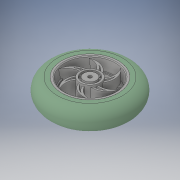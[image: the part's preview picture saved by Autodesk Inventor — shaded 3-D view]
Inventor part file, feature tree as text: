
AUTODESK INVENTOR PART (.ipt)
format: ipt  version: 2018 (Build 220112000, 112)  size: 624,640 bytes
history: native  units: in
note: dims shown in document units (in); Inventor stores cm internally (conversion verified against a paired STEP export)
features: sketch x11, extrude x9, plane x2, revolve x2, mirror x1, chamfer x1, projected_geometry x1
ambient origin geometry x8: Origin, YZ Plane, XZ Plane, XY Plane, X Axis, Y Axis, Z Axis, Center Point
bodies: Solid1 (feature_tree), Solid2 (feature_tree)
feature tree (27):
  extrude  "Extrusion1"  Depth=0.748in TaperAngle=0.0deg
  extrude  "Extrusion2"  Depth=0.748in TaperAngle=0.0deg
  extrude  "Extrusion3"  Depth=0.748in TaperAngle=0.0deg
  extrude  "Extrusion4"  Depth=0.748in TaperAngle=0.0deg
  plane  "Work Plane1"
  extrude  "Extrusion5"  Depth=0.6299in TaperAngle=0.0deg
  extrude  "Extrusion6"  Depth=0.2165in TaperAngle=0.0deg
  plane  "Work Plane2"
  mirror  "Mirror1"
  revolve  "Revolution1"  [1 undecoded]
  extrude  "Extrusion7"  Depth=0.0394in
  extrude  "Extrusion8"  TaperAngle=90.0deg  [1 undecoded]
  extrude  "Extrusion9"  Depth=0.5512in
  revolve  "Revolution2"  Angle=360.0deg
  chamfer  "Chamfer1"  Distance=0.0394in
  sketch  "Sketch1"  dims[d0=1.8504in d1=0.748in d2=0.0in]
  sketch  "Sketch2"  dims[d3=1.6732in d4=0.748in d5=0.0in]
  sketch  "Sketch3"  dims[d6=0.4134in d7=0.748in d8=0.0in]
  sketch  "Sketch4"  dims[d9=0.1181in d10=0.748in d11=0.0in]
  sketch  "Sketch5"  dims[d12=2.3622in d14=360.0deg d16=0.6299in d17=0.0in]
  sketch  "Sketch6"  dims[d18=2.3622in d20=360.0deg d22=0.2165in d23=0.0in]
  projected_geometry  "Projected Loop1"
  sketch  "Sketch7"  dims[d24=0.0787in d25=0.0197in]
  sketch  "Sketch8"  dims[d26=0.0197in d27=0.0394in]
  sketch  "Sketch9"  dims[d28=0.0394in d29=90.0deg]
  sketch  "Sketch10"  dims[d30=0.6693in d31=0.5512in]
  sketch  "Sketch11"  dims[d32=0.748in d33=0.0in d34=2.3622in d36=360.0deg d38=0.0394in d39=0.0in d40=0.0394in d41=0.0in d42=1.378in d43=90.0deg d44=0.0236in d45=0.0787in d46=45.0deg]
note: 2 required parameter values undecoded (feature->parameter linkage not recoverable at this tier; creation-order binding heuristic only, values carry confidence <= 0.55)